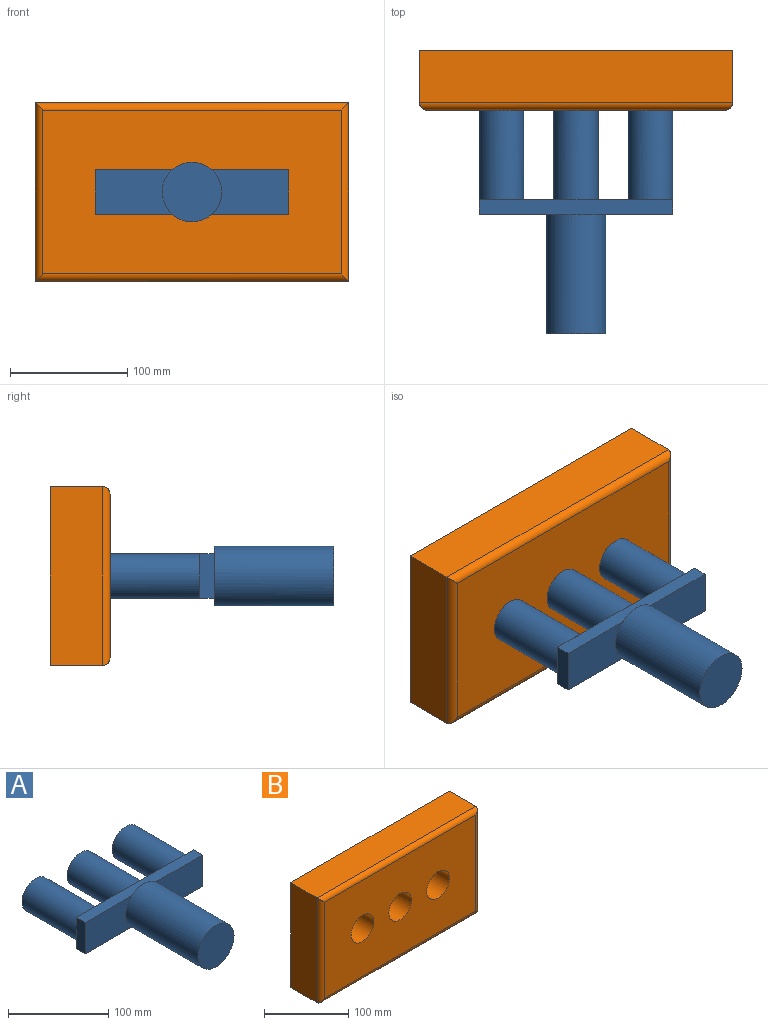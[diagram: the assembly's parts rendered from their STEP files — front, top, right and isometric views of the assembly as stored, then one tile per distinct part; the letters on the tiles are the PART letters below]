
ASSEMBLY  parts=2 mates=1
PART A: 22 faces, bbox 165.1x190.5x50.8 mm
  f0: plane 65.75x38.1mm, normal (0,-1,0), area 2278mm2, adj f6,f8,f9,f19
  f1: plane 19.05x19.05mm, normal (0,1,0), area 77.9mm2, adj f7,f8,f16
  f2: plane 19.05x19.05mm, normal (0,1,0), area 77.9mm2, adj f6,f7,f16
  f3: plane 19.05x19.05mm, normal (0,1,0), area 77.9mm2, adj f8,f9,f14
  f4: plane 63.5x38.1mm, normal (0,1,0), area 1279.3mm2, adj f6,f8,f12,f14
  f5: plane 63.5x38.1mm, normal (0,1,0), area 1279.3mm2, adj f6,f8,f12,f16
  f6: plane 165.1x12.7mm, normal (0,0,-1), area 2096.8mm2, adj f0,f2,f4,f5,f7,f9,f10,f11
  f7: plane 38.1x12.7mm, normal (1,0,0), area 483.9mm2, adj f1,f2,f6,f8,f10
  f8: plane 165.1x12.7mm, normal (0,0,1), area 2096.8mm2, adj f0,f1,f3,f4,f5,f7,f9,f10
  f9: plane 38.1x12.7mm, normal (-1,0,0), area 483.9mm2, adj f0,f3,f6,f8,f11
  f10: plane 65.75x38.1mm, normal (0,-1,0), area 2278mm2, adj f6,f7,f8,f19
  f11: plane 19.05x19.05mm, normal (0,1,0), area 77.9mm2, adj f6,f9,f14
  f12: cylinder r=19.05mm len=76.2mm, axis (0,-1,0), area 9120.7mm2, adj f4,f5,f13
  f13: plane 38.1x38.1mm, normal (0,1,0), area 1140.1mm2, adj f12
  f14: cylinder r=19.05mm len=76.2mm, axis (0,-1,0), area 9120.7mm2, adj f3,f4,f11,f15
  f15: plane 38.1x38.1mm, normal (0,1,0), area 1140.1mm2, adj f14
  f16: cylinder r=19.05mm len=76.2mm, axis (0,-1,0), area 9120.7mm2, adj f1,f2,f5,f17
  f17: plane 38.1x38.1mm, normal (0,1,0), area 1140.1mm2, adj f16
  f18: plane 33.6x6.35mm, normal (0,1,0), area 146.2mm2, adj f8,f19
  f19: cylinder r=25.4mm len=101.6mm, axis (0,1,0), area 16214.6mm2, adj f0,f10,f18,f20,f21
  f20: plane 50.8x50.8mm, normal (0,-1,0), area 2026.8mm2, adj f19
  f21: plane 33.6x6.35mm, normal (0,1,0), area 146.2mm2, adj f6,f19
PART B: 13 faces, bbox 266.7x50.8x152.4 mm
  f0: plane 266.7x44.45mm, normal (0,0,-1), area 11854.8mm2, adj f1,f6,f8,f9
  f1: plane 152.4x44.45mm, normal (1,0,0), area 6774.2mm2, adj f0,f2,f8,f10
  f2: plane 266.7x44.45mm, normal (0,0,1), area 11854.8mm2, adj f1,f6,f8,f12
  f3: cylinder r=19.05mm len=50.8mm, axis (0,1,0), area 6080.5mm2, adj f7,f8
  f4: cylinder r=19.05mm len=50.8mm, axis (0,1,0), area 6080.5mm2, adj f7,f8
  f5: cylinder r=19.05mm len=50.8mm, axis (0,1,0), area 6080.5mm2, adj f7,f8
  f6: plane 152.4x44.45mm, normal (-1,0,0), area 6774.2mm2, adj f0,f2,f8,f11
  f7: plane 254x139.7mm, normal (0,-1,0), area 32063.5mm2, adj f3,f4,f5,f9,f10,f11,f12
  f8: plane 266.7x152.4mm, normal (0,1,0), area 37224.8mm2, adj f0,f1,f2,f3,f4,f5,f6
  f9: cylinder r=6.35mm len=266.7mm, axis (-1,0,0), area 2614.2mm2, adj f0,f7,f10,f11
  f10: cylinder r=6.35mm len=152.4mm, axis (0,0,-1), area 1474.1mm2, adj f1,f7,f9,f12
  f11: cylinder r=6.35mm len=152.4mm, axis (0,0,1), area 1474.1mm2, adj f6,f7,f9,f12
  f12: cylinder r=6.35mm len=266.7mm, axis (1,0,0), area 2614.2mm2, adj f2,f7,f10,f11
PLACE A t=(131.86,-15.33,15.21)mm
PLACE B t=(131.86,111.67,15.21)mm
MATE slider A.f12 <-> B.f3  axis (0,1,0) through (131.86,60.87,15.21)mm
